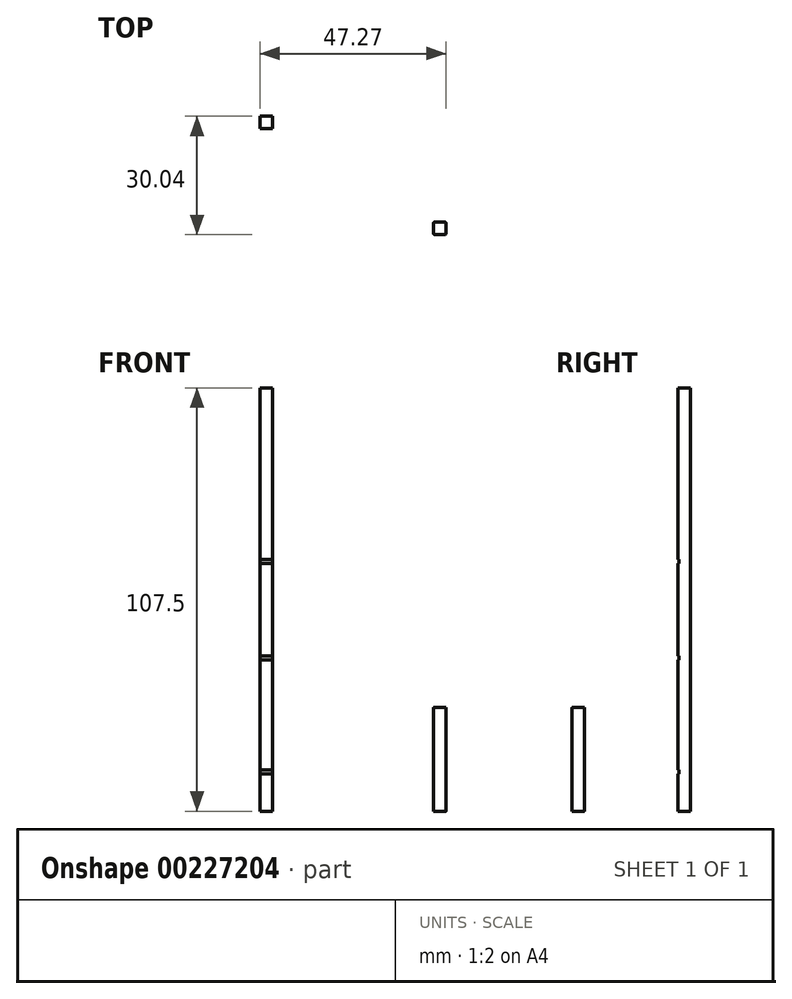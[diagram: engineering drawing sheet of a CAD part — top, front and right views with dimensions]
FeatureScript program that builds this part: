
annotation { "Feature Type Name" : "Feature", "Feature Type Description" : "" }
export const myFeature = defineFeature(function(context is Context, id is Id, definition is map)
    precondition{}
    {
        {
            var Q0;
            Q0=qCreatedBy(makeId("Top.planeOp"),FACE);
            var sketch = newSketch(context, id + "F0", { "sketchPlane" : qUnion([Q0])});
            skLineSegment(sketch, "E0.bottom", {"start": v(1.57, 1.58) * mm, "end": v(-1.58, 1.58) * mm});
            skLineSegment(sketch, "E0.top", {"start": v(1.58, -1.58) * mm, "end": v(-1.57, -1.58) * mm});
            skLineSegment(sketch, "E0.left", {"start": v(1.57, 1.58) * mm, "end": v(1.58, -1.58) * mm});
            skLineSegment(sketch, "E0.right", {"start": v(-1.58, 1.58) * mm, "end": v(-1.57, -1.58) * mm});
            skPoint(sketch, "E0.middle", {"position": v(0, 0) * mm});
            skLineSegment(sketch, "E1.bottom", {"start": v(-42.55, 28.47) * mm, "end": v(-45.7, 28.47) * mm});
            skLineSegment(sketch, "E1.top", {"start": v(-42.55, 25.32) * mm, "end": v(-45.7, 25.32) * mm});
            skLineSegment(sketch, "E1.left", {"start": v(-42.55, 28.47) * mm, "end": v(-42.55, 25.32) * mm});
            skLineSegment(sketch, "E1.right", {"start": v(-45.7, 28.47) * mm, "end": v(-45.7, 25.32) * mm});
            skPoint(sketch, "E1.middle", {"position": v(-44.12, 26.9) * mm});
            skSolve(sketch);
        }
        {
            var Q0;
            Q0=makeQuery(id+"F0.imprint","IMPRINT",FACE,{"disambiguationData":[TD([[makeQuery(id+"F0.imprint","IMPRINT",EDGE,{"derivedFrom":sQuery(id+"F0.wireOp",EDGE,"E0.bottom")}),1.0]])]});
            extrude(context, id + "F1", {"entities" : qUnion([Q0]), "depth" : 26.3 * mm});
        }
        {
            var Q0;
            Q0=makeQuery(id+"F1.opExtrude","SWEPT_EDGE",EDGE,{"disambiguationData":[OSD([sQuery(id+"F0.wireOp",EDGE,"E0.top"),sQuery(id+"F0.wireOp",EDGE,"E0.right")])]});
            var Q1;
            Q1=makeQuery(id+"F1.opExtrude","SWEPT_EDGE",EDGE,{"disambiguationData":[OSD([sQuery(id+"F0.wireOp",EDGE,"E0.top"),sQuery(id+"F0.wireOp",EDGE,"E0.left")])]});
            var Q2;
            Q2=makeQuery(id+"F1.opExtrude","SWEPT_EDGE",EDGE,{"disambiguationData":[OSD([sQuery(id+"F0.wireOp",EDGE,"E0.bottom"),sQuery(id+"F0.wireOp",EDGE,"E0.left")])]});
            var Q3;
            Q3=makeQuery(id+"F1.opExtrude","SWEPT_EDGE",EDGE,{"disambiguationData":[OSD([sQuery(id+"F0.wireOp",EDGE,"E0.bottom"),sQuery(id+"F0.wireOp",EDGE,"E0.right")])]});
            fillet(context, id + "F2", {"entities" : qUnion([Q0, Q1, Q2, Q3]), "radius" : 0.25 * mm, "tangentPropagation" : true, "allowEdgeOverflow" : false});
        }
        {
            var Q0;
            Q0=makeQuery(id+"F0.imprint","IMPRINT",FACE,{"disambiguationData":[TD([[makeQuery(id+"F0.imprint","IMPRINT",EDGE,{"derivedFrom":sQuery(id+"F0.wireOp",EDGE,"E1.bottom")}),1.0]])]});
            extrude(context, id + "F3", {"entities" : qUnion([Q0]), "depth" : 107.5 * mm});
        }
        {
            var Q0;
            Q0=makeQuery(id+"F3.opExtrude","SWEPT_FACE",FACE,{"disambiguationData":[OSD([sQuery(id+"F0.wireOp",EDGE,"E1.top")])]});
            var sketch = newSketch(context, id + "F4", { "sketchPlane" : qUnion([Q0])});
            skLineSegment(sketch, "E2", {"start": v(-45.7, 10.47) * mm, "end": v(-42.55, 10.47) * mm});
            skLineSegment(sketch, "E3", {"start": v(-45.7, 10.47) * mm, "end": v(-45.7, 9.47) * mm});
            skLineSegment(sketch, "E4", {"start": v(-45.7, 9.47) * mm, "end": v(-42.55, 9.47) * mm});
            skLineSegment(sketch, "E5", {"start": v(-42.55, 9.47) * mm, "end": v(-42.55, 10.47) * mm});
            skLineSegment(sketch, "E6", {"start": v(-45.7, 63.9) * mm, "end": v(-42.55, 63.9) * mm});
            skLineSegment(sketch, "E7", {"start": v(-45.7, 62.9) * mm, "end": v(-42.55, 62.9) * mm});
            skLineSegment(sketch, "E8", {"start": v(-45.7, 39.4) * mm, "end": v(-42.55, 39.4) * mm});
            skLineSegment(sketch, "E9", {"start": v(-45.7, 38.4) * mm, "end": v(-42.55, 38.4) * mm});
            skSolve(sketch);
        }
        {
            var Q0;
            Q0=makeQuery(id+"F4.imprint","IMPRINT",FACE,{"disambiguationData":[TD([[makeQuery(id+"F4.imprint","IMPRINT",EDGE,{"derivedFrom":sQuery(id+"F4.wireOp",EDGE,"E2")}),-1.0]])]});
            var Q1;
            {var subQ0=sQuery(id+"F4.wireOp",EDGE,"E8");Q1=makeQuery(id+"F4.imprint","IMPRINT",FACE,{"disambiguationData":[TD([[makeQuery(id+"F4.imprint","IMPRINT",EDGE,{"derivedFrom":subQ0}),-1.0]])]});}
            var Q2;
            {var subQ0=sQuery(id+"F4.wireOp",EDGE,"E6");Q2=makeQuery(id+"F4.imprint","IMPRINT",FACE,{"disambiguationData":[TD([[makeQuery(id+"F4.imprint","IMPRINT",EDGE,{"derivedFrom":subQ0}),-1.0]])]});}
            extrude(context, id + "F5", {"entities" : qUnion([Q0, Q1, Q2]), "operationType" : NewBodyOperationType.REMOVE, "oppositeDirection" : true, "depth" : 0.25 * mm});
        }
    });
